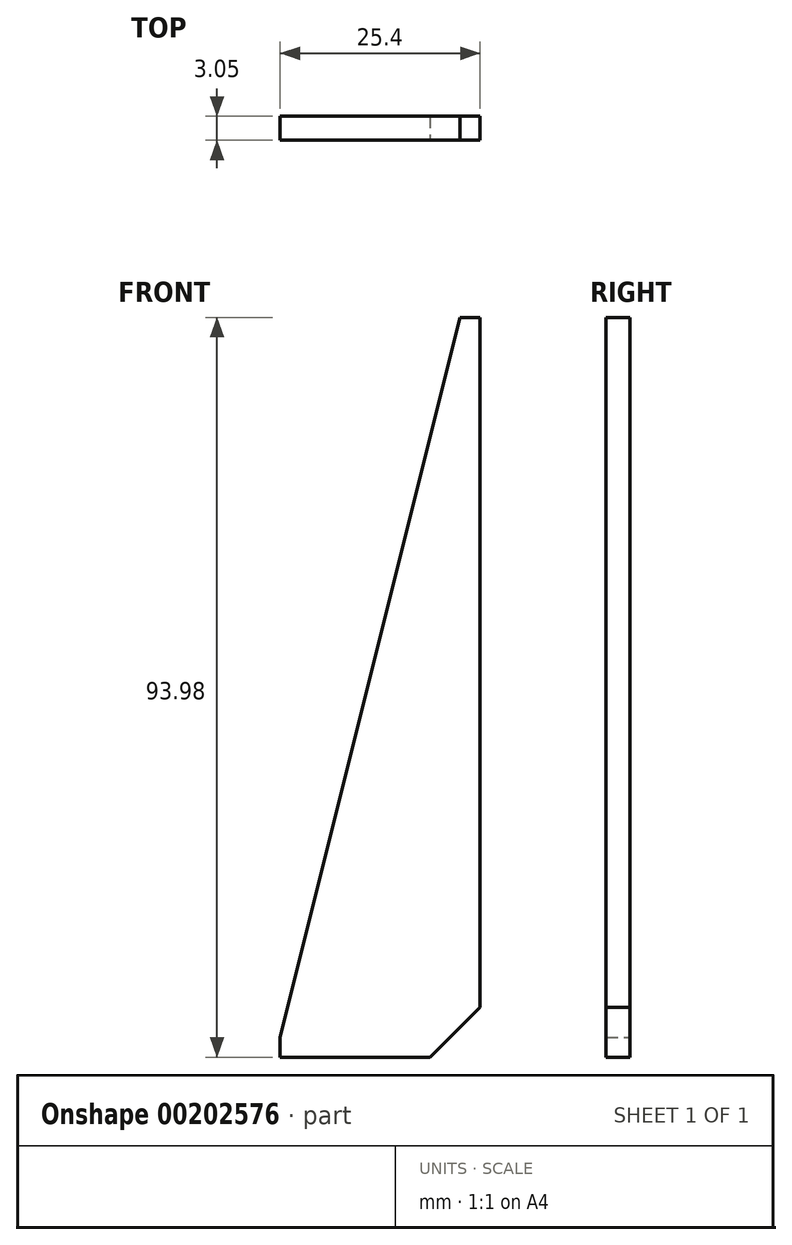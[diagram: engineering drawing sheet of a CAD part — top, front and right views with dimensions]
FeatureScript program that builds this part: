
annotation { "Feature Type Name" : "Feature", "Feature Type Description" : "" }
export const myFeature = defineFeature(function(context is Context, id is Id, definition is map)
    precondition{}
    {
        {
            var Q0;
            Q0=qCreatedBy(makeId("Front.planeOp"),FACE);
            var sketch = newSketch(context, id + "F0", { "sketchPlane" : qUnion([Q0])});
            skLineSegment(sketch, "E0.bottom", {"start": v(-12.7, 46.99) * mm, "end": v(12.7, 46.99) * mm});
            skLineSegment(sketch, "E0.top", {"start": v(-12.7, -47) * mm, "end": v(12.7, -47) * mm});
            skLineSegment(sketch, "E0.left", {"start": v(-12.7, 47) * mm, "end": v(-12.7, -47) * mm});
            skLineSegment(sketch, "E0.right", {"start": v(12.7, 47) * mm, "end": v(12.7, -47) * mm});
            skSolve(sketch);
        }
        {
            var Q0;
            Q0=makeQuery(id+"F0.imprint","IMPRINT",FACE,{"disambiguationData":[TD([[makeQuery(id+"F0.imprint","IMPRINT",EDGE,{"derivedFrom":sQuery(id+"F0.wireOp",EDGE,"E0.bottom")}),-1.0]])]});
            extrude(context, id + "F1", {"entities" : qUnion([Q0]), "depth" : 3.05 * mm});
        }
        {
            var Q0;
            Q0=makeQuery(id+"F1.opExtrude","SWEPT_EDGE",EDGE,{"disambiguationData":[OSD([sQuery(id+"F0.wireOp",EDGE,"E0.bottom"),sQuery(id+"F0.wireOp",EDGE,"E0.left")])]});
            chamfer(context, id + "F2", {"entities" : qUnion([Q0]), "chamferType" : ChamferType.TWO_OFFSETS, "width1" : 22.86 * mm, "oppositeDirection" : true, "width2" : 91.44 * mm, "tangentPropagation" : true});
        }
        {
            var Q0;
            Q0=makeQuery(id+"F1.opExtrude","SWEPT_EDGE",EDGE,{"disambiguationData":[OSD([sQuery(id+"F0.wireOp",EDGE,"E0.top"),sQuery(id+"F0.wireOp",EDGE,"E0.right")])]});
            chamfer(context, id + "F3", {"entities" : qUnion([Q0]), "chamferType" : ChamferType.OFFSET_ANGLE, "width" : 6.35 * mm, "oppositeDirection" : false, "angle" : 45 * degree, "tangentPropagation" : true});
        }
    });
